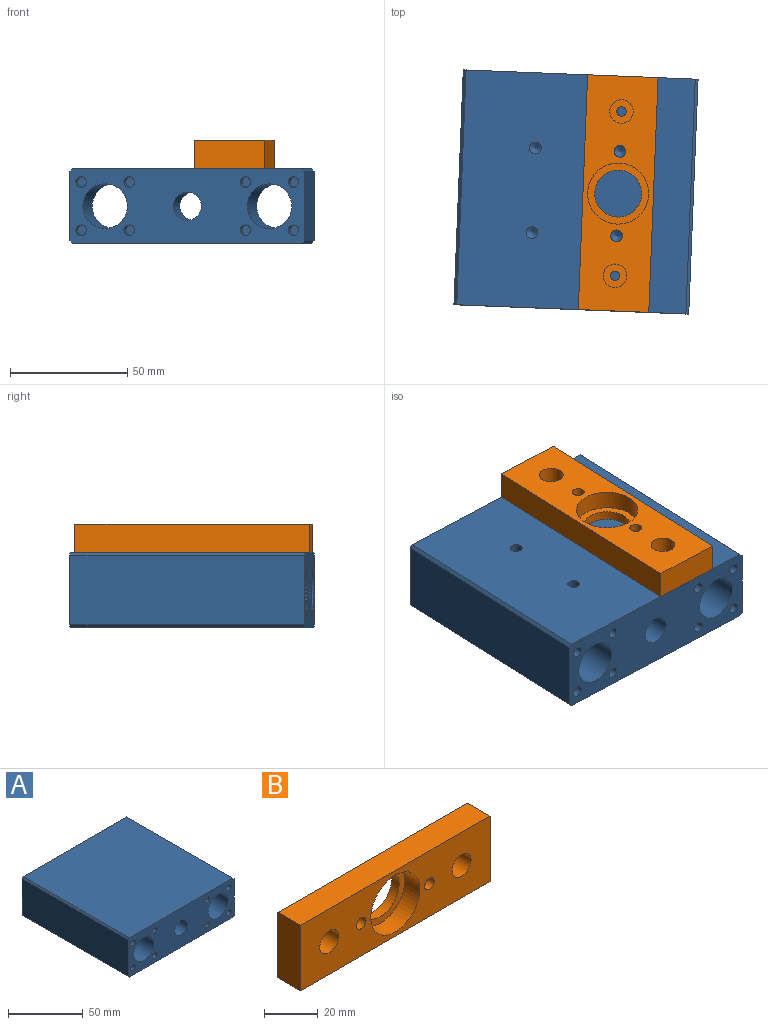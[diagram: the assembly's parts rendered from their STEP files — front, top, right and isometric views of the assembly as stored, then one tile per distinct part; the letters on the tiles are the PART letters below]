
ASSEMBLY  parts=2 mates=1
PART A: 63 faces, bbox 100x100x32 mm
  f0: plane 100x29.6mm, normal (-1,0,0), area 2960mm2, adj f6,f7,f11,f13
  f1: plane 100x97.6mm, normal (0,0,-1), area 9681.5mm2, adj f6,f7,f13,f14,f56,f58,f60,f62
  f2: plane 100x29.6mm, normal (1,0,0), area 2960mm2, adj f6,f7,f12,f14
  f3: cylinder r=9.5mm len=100mm, axis (0,1,0), area 5968.8mm2, adj f6,f7
  f4: plane 100x97.6mm, normal (0,0,1), area 9760mm2, adj f6,f7,f11,f12
  f5: cylinder r=9.5mm len=100mm, axis (0,1,0), area 5968.8mm2, adj f6,f7
  f6: plane 100x32mm, normal (0,-1,0), area 2389.8mm2, adj f0,f1,f2,f3,f4,f5,f8,f11
  f7: plane 100x32mm, normal (0,1,0), area 2209.9mm2, adj f0,f1,f2,f3,f4,f5,f10,f11
  f8: cylinder r=6mm len=70mm, axis (0,1,0), area 2638.9mm2, adj f6,f9
  f9: plane 18x18mm, normal (0,1,0), area 141.4mm2, adj f8,f10
  f10: cylinder r=9mm len=30mm, axis (0,1,0), area 1696.5mm2, adj f7,f9
  f11: plane 100x1.2mm, normal (-0.71,0,0.71), area 169.7mm2, adj f0,f4,f6,f7
  f12: plane 100x1.2mm, normal (0.71,0,0.71), area 169.7mm2, adj f2,f4,f6,f7
  f13: plane 100x1.2mm, normal (-0.71,0,-0.71), area 169.7mm2, adj f0,f1,f6,f7
  f14: plane 100x1.2mm, normal (0.71,0,-0.71), area 169.7mm2, adj f1,f2,f6,f7
  f15: cone r=0mm half-angle=59deg, axis (0,1,0), area 11.2mm2, adj f16
  f16: cylinder r=1.75mm len=20mm, axis (0,1,0), area 219.9mm2, adj f7,f15
  f17: cone r=0mm half-angle=59deg, axis (0,1,0), area 11.2mm2, adj f18
  f18: cylinder r=1.75mm len=20mm, axis (0,1,0), area 219.9mm2, adj f7,f17
  f19: cone r=0mm half-angle=59deg, axis (0,1,0), area 11.2mm2, adj f20
  f20: cylinder r=1.75mm len=20mm, axis (0,1,0), area 219.9mm2, adj f7,f19
  f21: cone r=0mm half-angle=59deg, axis (0,1,0), area 11.2mm2, adj f22
  f22: cylinder r=1.75mm len=20mm, axis (0,1,0), area 219.9mm2, adj f7,f21
  f23: cone r=0mm half-angle=59deg, axis (0,1,0), area 18.6mm2, adj f24
  f24: cylinder r=2.25mm len=20mm, axis (0,1,0), area 282.7mm2, adj f7,f23
  f25: cone r=0mm half-angle=59deg, axis (0,1,0), area 18.6mm2, adj f26
  f26: cylinder r=2.25mm len=20mm, axis (0,1,0), area 282.7mm2, adj f7,f25
  f27: cone r=0mm half-angle=59deg, axis (0,1,0), area 18.6mm2, adj f28
  f28: cylinder r=2.25mm len=20mm, axis (0,1,0), area 282.7mm2, adj f7,f27
  f29: cone r=0mm half-angle=59deg, axis (0,1,0), area 18.6mm2, adj f30
  f30: cylinder r=2.25mm len=20mm, axis (0,1,0), area 282.7mm2, adj f7,f29
  f31: cone r=0mm half-angle=59deg, axis (0,1,0), area 18.6mm2, adj f32
  f32: cylinder r=2.25mm len=20mm, axis (0,1,0), area 282.7mm2, adj f7,f31
  f33: cone r=0mm half-angle=59deg, axis (0,1,0), area 18.6mm2, adj f34
  f34: cylinder r=2.25mm len=20mm, axis (0,1,0), area 282.7mm2, adj f7,f33
  f35: cone r=0mm half-angle=59deg, axis (0,1,0), area 18.6mm2, adj f36
  f36: cylinder r=2.25mm len=20mm, axis (0,1,0), area 282.7mm2, adj f7,f35
  f37: cone r=0mm half-angle=59deg, axis (0,1,0), area 18.6mm2, adj f38
  f38: cylinder r=2.25mm len=20mm, axis (0,1,0), area 282.7mm2, adj f7,f37
  f39: cylinder r=2.25mm len=20mm, axis (0,-1,0), area 282.7mm2, adj f6,f40
  f40: plane 4.5x4.5mm, normal (0,-1,0), area 15.9mm2, adj f39
  f41: cylinder r=2.25mm len=20mm, axis (0,-1,0), area 282.7mm2, adj f6,f42
  f42: plane 4.5x4.5mm, normal (0,-1,0), area 15.9mm2, adj f41
  f43: cylinder r=2.25mm len=20mm, axis (0,-1,0), area 282.7mm2, adj f6,f44
  f44: plane 4.5x4.5mm, normal (0,-1,0), area 15.9mm2, adj f43
  f45: cylinder r=2.25mm len=20mm, axis (0,-1,0), area 282.7mm2, adj f6,f46
  f46: plane 4.5x4.5mm, normal (0,-1,0), area 15.9mm2, adj f45
  f47: cylinder r=2.25mm len=20mm, axis (0,-1,0), area 282.7mm2, adj f6,f48
  f48: plane 4.5x4.5mm, normal (0,-1,0), area 15.9mm2, adj f47
  f49: cylinder r=2.25mm len=20mm, axis (0,-1,0), area 282.7mm2, adj f6,f50
  f50: plane 4.5x4.5mm, normal (0,-1,0), area 15.9mm2, adj f49
  f51: cylinder r=2.25mm len=20mm, axis (0,-1,0), area 282.7mm2, adj f6,f52
  f52: plane 4.5x4.5mm, normal (0,-1,0), area 15.9mm2, adj f51
  f53: cylinder r=2.25mm len=20mm, axis (0,-1,0), area 282.7mm2, adj f6,f54
  f54: plane 4.5x4.5mm, normal (0,-1,0), area 15.9mm2, adj f53
  f55: cone r=0mm half-angle=59deg, axis (0,0,-1), area 22.9mm2, adj f56
  f56: cylinder r=2.5mm len=25mm, axis (0,0,-1), area 392.7mm2, adj f1,f55
  f57: cone r=0mm half-angle=59deg, axis (0,0,-1), area 22.9mm2, adj f58
  f58: cylinder r=2.5mm len=25mm, axis (0,0,-1), area 392.7mm2, adj f1,f57
  f59: cone r=0mm half-angle=59deg, axis (0,0,-1), area 22.9mm2, adj f60
  f60: cylinder r=2.5mm len=25mm, axis (0,0,-1), area 392.7mm2, adj f1,f59
  f61: cone r=0mm half-angle=59deg, axis (0,0,-1), area 22.9mm2, adj f62
  f62: cylinder r=2.5mm len=25mm, axis (0,0,-1), area 392.7mm2, adj f1,f61
PART B: 17 faces, bbox 100x12x30 mm
  f0: plane 30x12mm, normal (-1,0,0), area 360mm2, adj f1,f4,f6,f7
  f1: plane 100x12mm, normal (0,0,-1), area 1200mm2, adj f0,f2,f6,f7
  f2: plane 30x12mm, normal (1,0,0), area 360mm2, adj f1,f4,f6,f7
  f3: cylinder r=2.5mm len=12mm, axis (0,1,0), area 188.5mm2, adj f6,f7
  f4: plane 100x12mm, normal (0,0,1), area 1200mm2, adj f0,f2,f6,f7
  f5: cylinder r=2.5mm len=12mm, axis (0,1,0), area 188.5mm2, adj f6,f7
  f6: plane 100x30mm, normal (0,-1,0), area 2272.7mm2, adj f0,f1,f2,f3,f4,f5,f10,f13
  f7: plane 100x30mm, normal (0,1,0), area 2621.4mm2, adj f0,f1,f2,f3,f4,f5,f8,f11
  f8: cylinder r=10mm len=20mm, axis (0,-1,0), area 251.3mm2, adj f7,f9
  f9: plane 26x26mm, normal (0,-1,0), area 216.8mm2, adj f8,f10
  f10: cylinder r=13mm len=26mm, axis (0,-1,0), area 653.5mm2, adj f6,f9
  f11: cylinder r=2mm len=4mm, axis (0,-1,0), area 25.1mm2, adj f7,f12
  f12: plane 10x10mm, normal (0,-1,0), area 66mm2, adj f11,f13
  f13: cylinder r=5mm len=10mm, axis (0,-1,0), area 314.2mm2, adj f6,f12
  f14: cylinder r=2mm len=4mm, axis (0,-1,0), area 25.1mm2, adj f7,f15
  f15: plane 10x10mm, normal (0,-1,0), area 66mm2, adj f14,f16
  f16: cylinder r=5mm len=10mm, axis (0,-1,0), area 314.2mm2, adj f6,f15
PLACE A rot(axis=(0.02,1,0),180deg) t=(1.48,107.64,7.72)mm
PLACE B rot(axis=(-0.56,0.58,-0.58),121.3deg) t=(17.45,56.97,23.72)mm
MATE fastened A.f55 <-> B.f3  axis (0,0,1) through (16.76,38.98,23.72)mm
